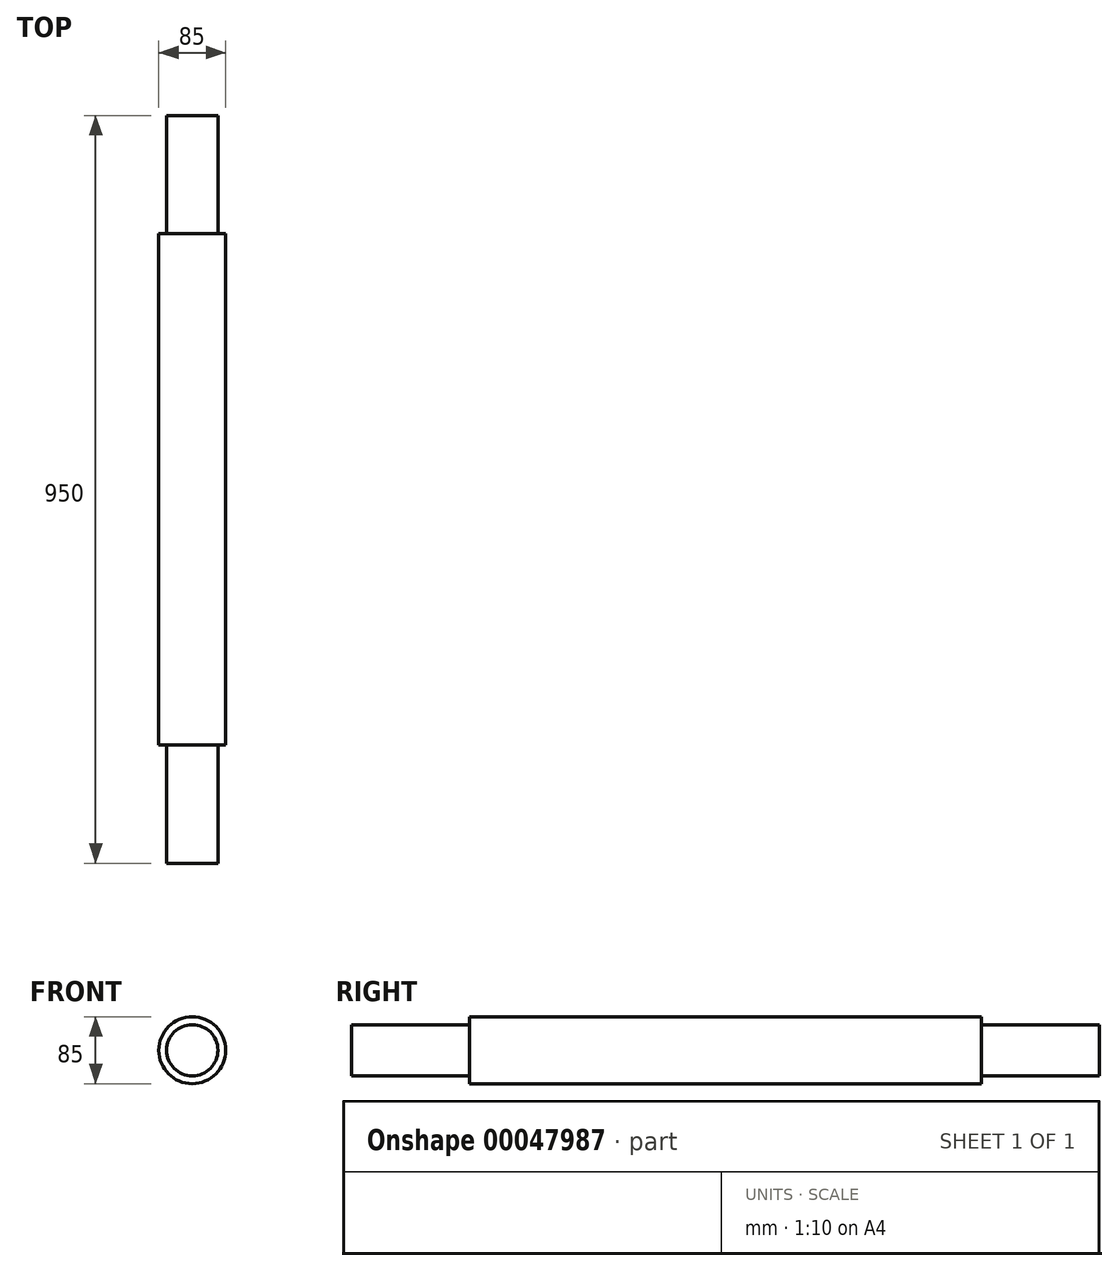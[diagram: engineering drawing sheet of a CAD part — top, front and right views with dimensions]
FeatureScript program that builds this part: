
annotation { "Feature Type Name" : "Feature", "Feature Type Description" : "" }
export const myFeature = defineFeature(function(context is Context, id is Id, definition is map)
    precondition{}
    {
        {
            var Q0;
            Q0=qCreatedBy(makeId("Front.planeOp"),FACE);
            var sketch = newSketch(context, id + "F0", { "sketchPlane" : qUnion([Q0])});
            skCircle(sketch, "E0", {"center": v(0, 0) * mm, "radius": 32.5 * mm});
            skSolve(sketch);
        }
        {
            var Q0;
            Q0=makeQuery(id+"F0.imprint","IMPRINT",FACE,{"disambiguationData":[TD([[makeQuery(id+"F0.imprint","IMPRINT",EDGE,{"derivedFrom":sQuery(id+"F0.wireOp",EDGE,"E0")}),1.0]])]});
            extrude(context, id + "F1", {"entities" : qUnion([Q0]), "depth" : 150 * mm});
        }
        {
            var Q0;
            Q0=makeQuery(id+"F1.opExtrude","CAP_FACE",FACE,{"disambiguationData":[OSD([sQuery(id+"F0.wireOp",EDGE,"E0")])],"isStart":false});
            var sketch = newSketch(context, id + "F2", { "sketchPlane" : qUnion([Q0])});
            skCircle(sketch, "E1", {"center": v(0, 0) * mm, "radius": 42.5 * mm});
            skSolve(sketch);
        }
        {
            var Q0;
            Q0=makeQuery(id+"F2.imprint","IMPRINT",FACE,{"disambiguationData":[TD([[makeQuery(id+"F2.imprint","IMPRINT",EDGE,{"derivedFrom":sQuery(id+"F2.wireOp",EDGE,"E1")}),1.0]])]});
            var Q1;
            Q1=makeQuery(id+"F2.imprint","IMPRINT",FACE,{"disambiguationData":[TD([[makeQuery(id+"F2.imprint","IMPRINT",EDGE,{"derivedFrom":makeQuery(id+"F1.opExtrude","CAP_EDGE",EDGE,{"disambiguationData":[OSD([sQuery(id+"F0.wireOp",EDGE,"E0")])],"isStart":false})}),1.0]])]});
            extrude(context, id + "F3", {"entities" : qUnion([Q0, Q1]), "operationType" : NewBodyOperationType.ADD, "depth" : 650 * mm});
        }
        {
            var Q0;
            Q0=makeQuery(id+"F3.opExtrude","CAP_FACE",FACE,{"disambiguationData":[OSD([sQuery(id+"F2.wireOp",EDGE,"E1")])],"isStart":false});
            var sketch = newSketch(context, id + "F4", { "sketchPlane" : qUnion([Q0])});
            skCircle(sketch, "E2", {"center": v(0, 0) * mm, "radius": 32.5 * mm});
            skSolve(sketch);
        }
        {
            var Q0;
            Q0=makeQuery(id+"F4.imprint","IMPRINT",FACE,{"disambiguationData":[TD([[makeQuery(id+"F4.imprint","IMPRINT",EDGE,{"derivedFrom":sQuery(id+"F4.wireOp",EDGE,"E2")}),1.0]])]});
            extrude(context, id + "F5", {"entities" : qUnion([Q0]), "operationType" : NewBodyOperationType.ADD, "depth" : 150 * mm});
        }
    });
